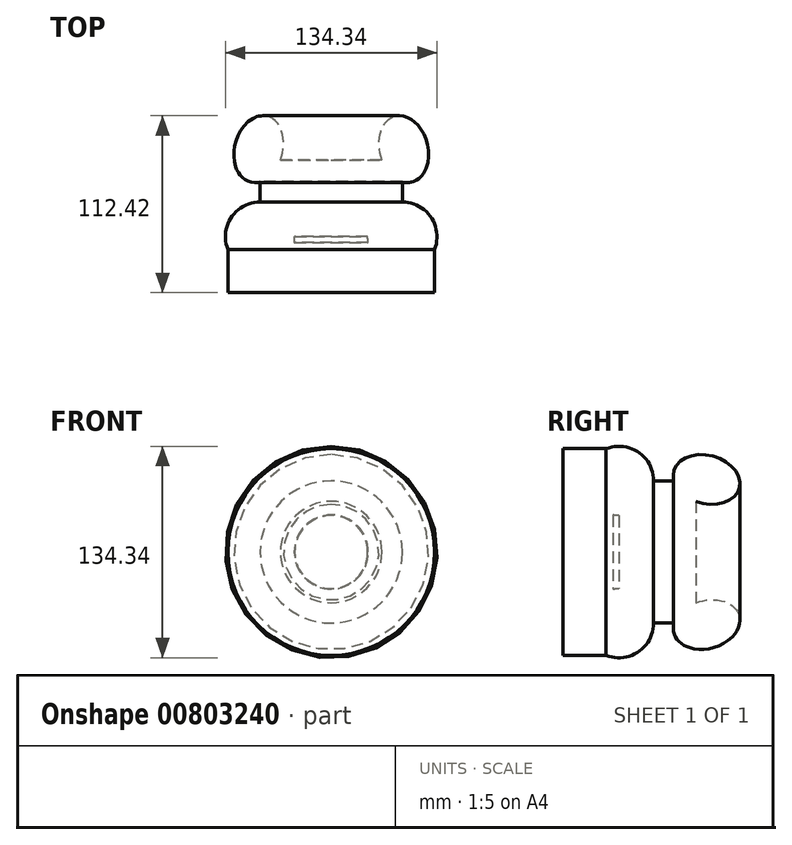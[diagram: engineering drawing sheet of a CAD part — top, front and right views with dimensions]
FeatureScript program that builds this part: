
annotation { "Feature Type Name" : "Feature", "Feature Type Description" : "" }
export const myFeature = defineFeature(function(context is Context, id is Id, definition is map)
    precondition{}
    {
        {
            var Q0;
            Q0=qCreatedBy(makeId("Top.planeOp"),FACE);
            var sketch = newSketch(context, id + "F0", { "sketchPlane" : qUnion([Q0])});
            skLineSegment(sketch, "E0.bottom", {"start": v(0, 40.88) * mm, "end": v(32.24, 40.88) * mm});
            skLineSegment(sketch, "E0.top", {"start": v(0, -7.85) * mm, "end": v(23.17, -7.85) * mm});
            skLineSegment(sketch, "E0.left", {"start": v(0, 40.88) * mm, "end": v(0, -7.85) * mm});
            skLineSegment(sketch, "E0.right", {"start": v(45.17, 27.2) * mm, "end": v(45.17, 14.16) * mm});
            skLineSegment(sketch, "E1.bottom", {"start": v(0, -43.44) * mm, "end": v(65.6, -43.44) * mm});
            skLineSegment(sketch, "E1.top", {"start": v(0, -11.68) * mm, "end": v(23.5, -11.68) * mm});
            skLineSegment(sketch, "E1.left", {"start": v(0, -43.44) * mm, "end": v(0, -11.68) * mm});
            skLineSegment(sketch, "E1.right", {"start": v(65.6, -43.44) * mm, "end": v(65.6, -16) * mm});
            skArc(sketch, "E2", {"start": v(23.17, -7.85) * mm, "mid": v(23.25, -9.77) * mm, "end": v(23.5, -11.68) * mm});
            skEllipticalArc(sketch, "E3", {});
            skArc(sketch, "E4.trimOffspring", {"start": v(65.6, -16) * mm, "mid": v(63.38, 4.5) * mm, "end": v(45.17, 14.16) * mm});
            skLineSegment(sketch, "E5", {"start": v(0, 74.28) * mm, "end": v(0, -73.37) * mm, "construction": true});
            const initialGuessF0  = {"E3": [0.04608198627829552, 0.04781575873494148, 0.2544932396159926, -0.9670745529636053, 0.021513676500574147, 0.015315713074558488, 5.871291591730069, 4.860989802513313]};
            skSetInitialGuess(sketch, initialGuessF0);
            skSolve(sketch);
        }
        {
            var Q0;
            Q0=makeQuery(id+"F0.imprint","IMPRINT",FACE,{"disambiguationData":[TD([[makeQuery(id+"F0.imprint","IMPRINT",EDGE,{"derivedFrom":sQuery(id+"F0.wireOp",EDGE,"E0.bottom")}),-1.0]])]});
            var Q1;
            Q1=sQuery(id+"F0.wireOp",EDGE,"E5");
            revolve(context, id + "F1", {"surfaceOperationType" : NewSurfaceOperationType.NEW, "entities" : qUnion([Q0]), "axis" : qUnion([Q1]), "revolveType" : RevolveType.FULL});
        }
    });
